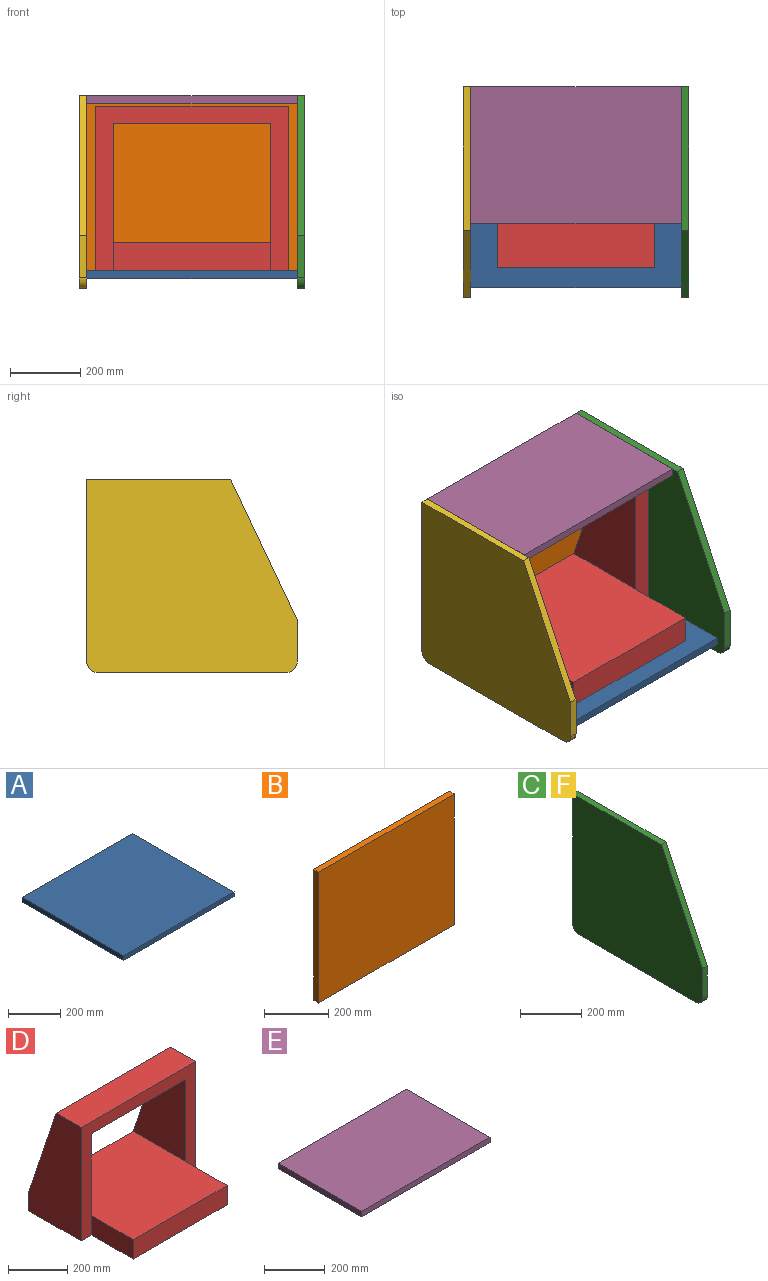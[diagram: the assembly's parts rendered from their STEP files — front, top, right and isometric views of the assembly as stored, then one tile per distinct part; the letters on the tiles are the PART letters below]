
ASSEMBLY  parts=6 mates=5
PART A: 6 faces, bbox 600x550x22 mm
  f0: plane 600x22mm, normal (0,-1,0), area 13200mm2, adj f1,f3,f4,f5
  f1: plane 550x22mm, normal (1,0,0), area 12100mm2, adj f0,f2,f4,f5
  f2: plane 600x22mm, normal (0,1,0), area 13200mm2, adj f1,f3,f4,f5
  f3: plane 550x22mm, normal (-1,0,0), area 12100mm2, adj f0,f2,f4,f5
  f4: plane 600x550mm, normal (0,0,1), area 330000mm2, adj f0,f1,f2,f3
  f5: plane 600x550mm, normal (0,0,-1), area 330000mm2, adj f0,f1,f2,f3
PART B: 6 faces, bbox 600x22x500 mm
  f0: plane 500x22mm, normal (1,0,0), area 11000mm2, adj f1,f3,f4,f5
  f1: plane 600x22mm, normal (0,0,1), area 13200mm2, adj f0,f2,f4,f5
  f2: plane 500x22mm, normal (-1,0,0), area 11000mm2, adj f1,f3,f4,f5
  f3: plane 600x22mm, normal (0,0,-1), area 13200mm2, adj f0,f2,f4,f5
  f4: plane 600x500mm, normal (0,-1,0), area 300000mm2, adj f0,f1,f2,f3
  f5: plane 600x500mm, normal (0,1,0), area 300000mm2, adj f0,f1,f2,f3
PART C: 9 faces, bbox 22x600x550 mm
  f0: plane 520x22mm, normal (0,1,0), area 11440mm2, adj f1,f4,f5,f7
  f1: plane 410x22mm, normal (0,0,1), area 9020mm2, adj f0,f4,f5,f8
  f2: plane 120x22mm, normal (0,-1,0), area 2640mm2, adj f4,f5,f6,f8
  f3: plane 540x22mm, normal (0,0,-1), area 11880mm2, adj f4,f5,f6,f7
  f4: plane 600x550mm, normal (1,0,0), area 291613.7mm2, adj f0,f1,f2,f3,f6,f7,f8
  f5: plane 600x550mm, normal (-1,0,0), area 291613.7mm2, adj f0,f1,f2,f3,f6,f7,f8
  f6: cylinder r=30mm len=30mm, axis (1,0,0), area 1036.7mm2, adj f2,f3,f4,f5
  f7: cylinder r=30mm len=30mm, axis (-1,0,0), area 1036.7mm2, adj f0,f3,f4,f5
  f8: plane 400x190mm, normal (0,-0.9,0.43), area 9742.3mm2, adj f1,f2,f4,f5
PART D: 14 faces, bbox 550x450x470 mm
  f0: plane 470x250mm, normal (1,0,0), area 92150mm2, adj f4,f5,f6,f7,f8
  f1: plane 450x80mm, normal (0,-1,0), area 36000mm2, adj f3,f4,f12,f13
  f2: plane 470x250mm, normal (-1,0,0), area 92150mm2, adj f4,f5,f6,f7,f8
  f3: plane 450x450mm, normal (0,0,1), area 202500mm2, adj f1,f6,f9,f10,f12,f13
  f4: plane 550x450mm, normal (0,0,-1), area 227500mm2, adj f0,f1,f2,f6,f7,f12,f13
  f5: plane 550x390mm, normal (0,0.95,0.32), area 64826.7mm2, adj f0,f2,f6,f8,f9,f10,f11
  f6: plane 550x80mm, normal (0,1,0), area 44000mm2, adj f0,f2,f3,f4,f5
  f7: plane 550x470mm, normal (0,-1,0), area 69500mm2, adj f0,f2,f4,f8,f9,f10,f11,f12
  f8: plane 550x120mm, normal (0,0,1), area 66000mm2, adj f0,f2,f5,f7
  f9: plane 340x250mm, normal (1,0,0), area 65733.3mm2, adj f3,f5,f7,f11
  f10: plane 340x250mm, normal (-1,0,0), area 65733.3mm2, adj f3,f5,f7,f11
  f11: plane 450x136.67mm, normal (0,0,-1), area 61500mm2, adj f5,f7,f9,f10
  f12: plane 200x80mm, normal (1,0,0), area 16000mm2, adj f1,f3,f4,f7
  f13: plane 200x80mm, normal (-1,0,0), area 16000mm2, adj f1,f3,f4,f7
PART E: 6 faces, bbox 600x390x22 mm
  f0: plane 390x22mm, normal (1,0,0), area 8580mm2, adj f1,f3,f4,f5
  f1: plane 600x22mm, normal (0,1,0), area 13200mm2, adj f0,f2,f4,f5
  f2: plane 390x22mm, normal (-1,0,0), area 8580mm2, adj f1,f3,f4,f5
  f3: plane 600x22mm, normal (0,-1,0), area 13200mm2, adj f0,f2,f4,f5
  f4: plane 600x390mm, normal (0,0,1), area 234000mm2, adj f0,f1,f2,f3
  f5: plane 600x390mm, normal (0,0,-1), area 234000mm2, adj f0,f1,f2,f3
PART F: same geometry as C
PLACE A t=(-45.45,-24.85,18.31)mm fixed
PLACE B t=(-45.45,272.15,268.31)mm
PLACE C t=(254.55,-20.55,265.31)mm
PLACE D t=(-45.45,-18.74,40.31)mm
PLACE E t=(-45.45,77.15,518.31)mm
PLACE F t=(-367.45,-20.55,265.31)mm
MATE fastened C.f5 <-> A.f1  axis (-1,0,0) through (254.55,-27.55,-9.69)mm
MATE fastened E.f5 <-> B.f1  axis (0,0,-1) through (-45.45,272.15,518.31)mm
MATE fastened D.f4 <-> A.f4  axis (0,0,-1) through (-45.45,-7.75,40.31)mm
MATE fastened A.f3 <-> F.f4  axis (-1,0,0) through (-345.45,-24.85,18.31)mm
MATE fastened B.f4 <-> A.f2  axis (0,-1,0) through (-45.45,250.15,18.31)mm
